# Revit family: 8110346c-7eec-4701-892f-fd612e51d585
name_source: partatom
category: Pipe Fittings
revit_build: Autodesk Revit 2016 (Build: 20161004_0715(x64)
units: mm (PartAtom-declared; Revit-internal decimal feet)

## family parameters
Always vertical = Yes
Cut with Voids When Loaded = No
OmniClass Number = 23.60.30.11.14
OmniClass Title = Pipework Fittings
Part Type = Union
Round Connector Dimension = Use Radius
Shared = Yes
Work Plane-Based = No

## types (1)
- Standard
    04 CSI = 22 00 00
    95 CSI = 15100
    Assembly Code = D2090800
    CADworks URL = http://www.CADworks.net
    Clip Lock Angle = 35.48°
    Compression Liner Material = Rubber - Schott
    Coupling Band Material = Steel - Schott - Stainless
    Description = Drainline Coupling (Bead To Bead)
    K Coefficient Table = Reducer/Coupling/Union/Increaser
    Lookup Table Name = Coupling-Schott-Kimax-Drainline-Bead_to_Bead-6650
    Loss Method = K Coefficient from Table
    Manufacturer = SCHOTT
    Model = 6650-1500, 6650-2000, 6650-3000, 6650-4000, 6650-6000
    Product URL = http://www.us.schott.com
    Seal Ring Material = Teflon - Schott
    Series = Kimax
    Subcategory = Coupling
    URL = http://www.us.schott.com

## geometry (parser evidence)
native form markers: Blend x2, Sweep x2
no freeform markers — native parametric forms only
